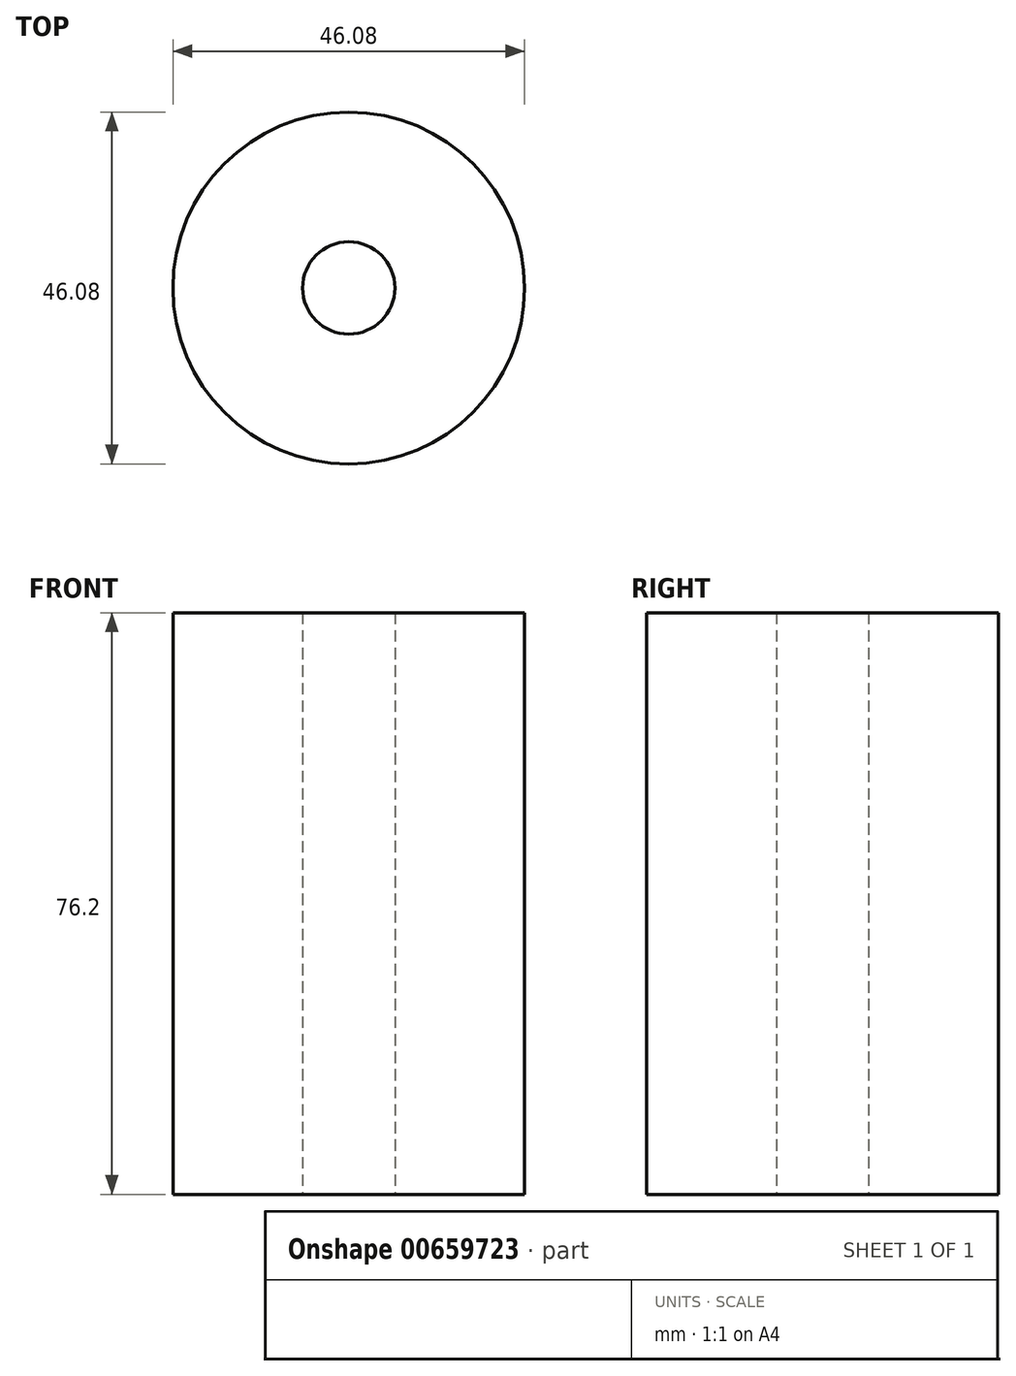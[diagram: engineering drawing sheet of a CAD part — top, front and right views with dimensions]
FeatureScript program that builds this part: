
annotation { "Feature Type Name" : "Feature", "Feature Type Description" : "" }
export const myFeature = defineFeature(function(context is Context, id is Id, definition is map)
    precondition{}
    {
        {
            var Q0;
            Q0=qCreatedBy(makeId("Top.planeOp"),FACE);
            var sketch = newSketch(context, id + "F0", { "sketchPlane" : qUnion([Q0])});
            skCircle(sketch, "E0", {"center": v(0, 0) * mm, "radius": 23.04 * mm});
            skSolve(sketch);
        }
        {
            var Q0;
            Q0=makeQuery(id+"F0.imprint","IMPRINT",FACE,{"disambiguationData":[TD([[makeQuery(id+"F0.imprint","IMPRINT",EDGE,{"derivedFrom":sQuery(id+"F0.wireOp",EDGE,"E0")}),1.0]])]});
            extrude(context, id + "F1", {"entities" : qUnion([Q0]), "depth" : 76.2 * mm, "offsetDistance" : 25.4 * mm});
        }
        {
            var Q0;
            Q0=makeQuery(id+"F1.opExtrude","CAP_FACE",FACE,{"disambiguationData":[OSD([sQuery(id+"F0.wireOp",EDGE,"E0")])],"isStart":true});
            var sketch = newSketch(context, id + "F2", { "sketchPlane" : qUnion([Q0])});
            skCircle(sketch, "E1", {"center": v(0, 0) * mm, "radius": 6.05 * mm});
            skSolve(sketch);
        }
        {
            var Q0;
            Q0=makeQuery(id+"F2.imprint","IMPRINT",FACE,{"disambiguationData":[TD([[makeQuery(id+"F2.imprint","IMPRINT",EDGE,{"derivedFrom":sQuery(id+"F2.wireOp",EDGE,"E1")}),1.0]])]});
            var Q1;
            Q1=sQuery(id+"F2.wireOp",EDGE,"E1");
            extrude(context, id + "F3", {"entities" : qUnion([Q0]), "operationType" : NewBodyOperationType.REMOVE, "surfaceEntities" : qUnion([Q1]), "oppositeDirection" : true, "depth" : 76.2 * mm, "offsetDistance" : 25.4 * mm});
        }
    });
